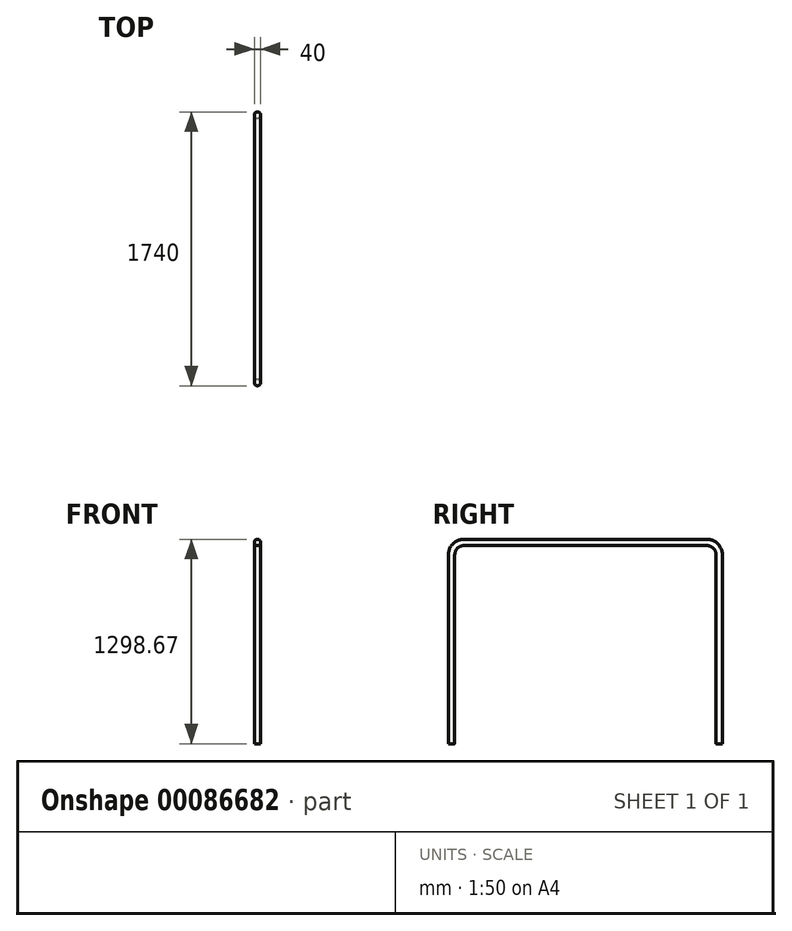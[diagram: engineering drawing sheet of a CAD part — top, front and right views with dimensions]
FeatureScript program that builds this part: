
annotation { "Feature Type Name" : "Feature", "Feature Type Description" : "" }
export const myFeature = defineFeature(function(context is Context, id is Id, definition is map)
    precondition{}
    {
        {
            var Q0;
            Q0=qCreatedBy(makeId("Right.planeOp"),FACE);
            var sketch = newSketch(context, id + "F0", { "sketchPlane" : qUnion([Q0])});
            skLineSegment(sketch, "E0", {"start": v(-861.68, 0) * mm, "end": v(-861.68, 1200) * mm});
            skLineSegment(sketch, "E1", {"start": v(-783, 1278.67) * mm, "end": v(759.65, 1278.67) * mm});
            skLineSegment(sketch, "E2", {"start": v(838.32, 1200) * mm, "end": v(838.32, 0) * mm});
            skPoint(sketch, "E3.visualSharp", {"position": v(-861.68, 1278.67) * mm});
            skArc(sketch, "E3.filletArc", {"start": v(-783, 1278.67) * mm, "mid": v(-838.63, 1255.63) * mm, "end": v(-861.68, 1200) * mm});
            skPoint(sketch, "E4.visualSharp", {"position": v(838.32, 1278.67) * mm});
            skArc(sketch, "E4.filletArc", {"start": v(838.32, 1200) * mm, "mid": v(815.28, 1255.63) * mm, "end": v(759.65, 1278.67) * mm});
            skSolve(sketch);
        }
        {
            var Q0;
            Q0=qCreatedBy(makeId("Top.planeOp"),FACE);
            var sketch = newSketch(context, id + "F1", { "sketchPlane" : qUnion([Q0])});
            skCircle(sketch, "E5", {"center": v(0, -861.68) * mm, "radius": 20 * mm});
            skSolve(sketch);
        }
        {
            var Q0;
            Q0=makeQuery(id+"F1.imprint","IMPRINT",FACE,{"disambiguationData":[TD([[makeQuery(id+"F1.imprint","IMPRINT",EDGE,{"derivedFrom":sQuery(id+"F1.wireOp",EDGE,"E5")}),1.0]])]});
            var Q1;
            Q1=sQuery(id+"F0.wireOp",EDGE,"E0");
            var Q2;
            Q2=sQuery(id+"F0.wireOp",EDGE,"E3.filletArc");
            var Q3;
            Q3=sQuery(id+"F0.wireOp",EDGE,"E1");
            var Q4;
            Q4=sQuery(id+"F0.wireOp",EDGE,"E4.filletArc");
            var Q5;
            Q5=sQuery(id+"F0.wireOp",EDGE,"E2");
            sweep(context, id + "F2", {"profiles" : qUnion([Q0]), "path" : qUnion([Q1, Q2, Q3, Q4, Q5])});
        }
    });
